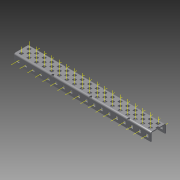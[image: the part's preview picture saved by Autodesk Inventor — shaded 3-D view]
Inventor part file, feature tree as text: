
AUTODESK INVENTOR PART (.ipt)
format: ipt  version: 2015 (Build 190159000, 159)  size: 2,116,096 bytes
history: native  units: in
note: dims shown in document units (in); Inventor stores cm internally (conversion verified against a paired STEP export)
features: other x96, pattern_linear x3, sheet_metal_op x1, extrude x1, imported_body x1, sketch x1
ambient origin geometry x8: Origin, YZ Plane, XZ Plane, XY Plane, X Axis, Y Axis, Z Axis, Center Point
bodies: Body1 (feature_tree)
feature tree (103):
  sheet_metal_op  "Fold1"
  other  "C-Channel"
  extrude  "length cut"  Depth=0.5in
  other  "top axis"
  other  "inner axis"
  other  "front axis"
  other  "back axis"
  pattern_linear  "top axes"  Spacing1=0.5in  [1 undecoded]
  pattern_linear  "inner axes"  Spacing1=0.5in  [1 undecoded]
  pattern_linear  "horiz axes"  Spacing1=-9.0in  [1 undecoded]
  other  "right plane"
  imported_body  "Base1"
  sketch  "Sketch1"  dims[d1=0.0in d4=0.5in d5=0.7874in d7=0.5in d10=0.5in d13=0.5in d14=-9.0in d15=0.0in d16=0.0in d17=0.0in d18=0.0in d19=0.0in]
  other  "Work Point1"
  other  "Work Point2"
  other  "Work Point3"
  other  "Work Point4"
  other  "Work Axis5"
  other  "Work Axis6"
  other  "Work Axis7"
  other  "Work Axis8"
  other  "Work Axis11"
  other  "Work Axis12"
  other  "Work Axis13"
  other  "Work Axis14"
  other  "Work Axis15"
  other  "Work Axis18"
  other  "Work Axis19"
  other  "Work Axis20"
  other  "Work Axis23"
  other  "Work Axis24"
  other  "Work Axis25"
  other  "Work Axis26"
  other  "Work Axis30"
  other  "Work Axis31"
  other  "Work Axis32"
  other  "Work Axis33"
  other  "left plane"
  other  "Work Axis37"
  other  "Work Axis38"
  other  "Work Axis39"
  other  "Work Axis40"
  other  "Work Axis41"
  other  "Work Axis42"
  other  "Work Axis43"
  other  "Work Axis44"
  other  "Work Axis45"
  other  "Work Axis46"
  other  "Work Axis57"
  other  "Work Axis58"
  other  "Work Axis59"
  other  "Work Axis60"
  other  "Work Axis61"
  other  "Work Axis62"
  other  "Work Axis63"
  other  "Work Axis64"
  other  "Work Axis65"
  other  "Work Axis66"
  other  "Work Axis77"
  other  "Work Axis78"
  other  "Work Axis79"
  other  "Work Axis80"
  other  "Work Axis81"
  other  "Work Axis82"
  other  "Work Axis83"
  other  "Work Axis84"
  other  "Work Axis85"
  other  "Work Axis86"
  other  "Work Axis97"
  other  "Work Axis98"
  other  "Work Axis99"
  other  "Work Axis100"
  other  "Work Axis101"
  other  "Work Axis102"
  other  "Work Axis103"
  other  "Work Axis104"
  other  "Work Axis105"
  other  "Work Axis106"
  other  "Work Axis117"
  other  "Work Axis118"
  other  "Work Axis119"
  other  "Work Axis120"
  other  "Work Axis121"
  other  "Work Axis122"
  other  "Work Axis123"
  other  "Work Axis124"
  other  "Work Axis125"
  other  "Work Axis126"
  other  "Work Axis137"
  other  "Work Axis138"
  other  "Work Axis139"
  other  "Work Axis140"
  other  "Work Axis141"
  other  "Work Axis142"
  other  "Work Axis143"
  other  "Work Axis144"
  other  "Work Axis145"
  other  "Work Axis146"
  other  "Work Axis147"
  other  "Work Axis148"
  other  "Work Axis149"
  other  "Work Axis150"
  other  "Work Axis151"
note: 3 required parameter values undecoded (feature->parameter linkage not recoverable at this tier; creation-order binding heuristic only, values carry confidence <= 0.55)
